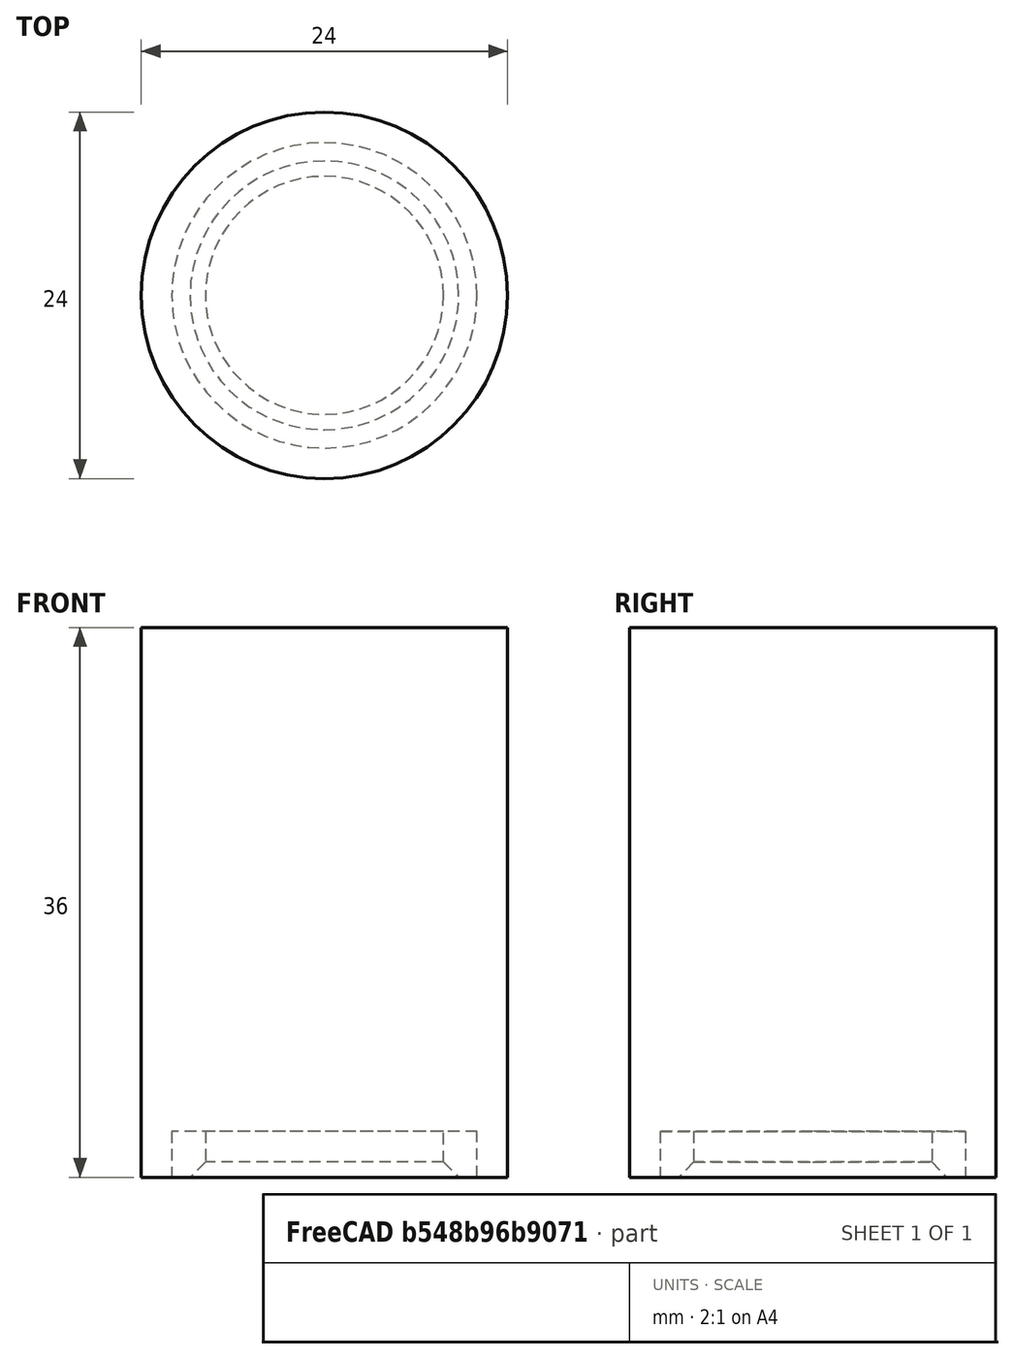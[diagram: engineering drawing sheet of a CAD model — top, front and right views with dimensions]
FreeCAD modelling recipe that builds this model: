
FCSTD DOCUMENT  (FreeCAD 0.20R25645 (Git))
Label: Brake Liquid Tester lid
License: All rights reserved
LicenseURL: http://en.wikipedia.org/wiki/All_rights_reserved
objects: Part::Cylinder×4, Part::Cut×2, Part::Chamfer×2, Part::MultiFuse×1, Part::Box×1
note: 10 computed .brp shape members not serialized (recipe doc carries the construction recipe); baked Part::Feature solids carry a one-line shape summary decoded from their .brp

FEATURE [Part::Cylinder] Cylinder
  Angle = 360
  AttacherType = Attacher::AttachEngine3D
  FirstAngle = 0
  Height = 28
  Radius = 10
  SecondAngle = 0
FEATURE [Part::Cylinder] Cylinder001
  Angle = 360
  AttacherType = Attacher::AttachEngine3D
  FirstAngle = 0
  Height = 12
  Radius = 7.8
  SecondAngle = 0
FEATURE [Part::Cylinder] Cylinder002
  Angle = 360
  AttacherType = Attacher::AttachEngine3D
  FirstAngle = 0
  Height = 12
  Placement = pos=(0,0,12) rot=(0,0,1;0rad)
  Radius = 5
  SecondAngle = 0
FEATURE [Part::Cylinder] Cylinder003
  Angle = 360
  AttacherType = Attacher::AttachEngine3D
  FirstAngle = 0
  Height = 36
  Radius = 12
  SecondAngle = 0
FEATURE [Part::MultiFuse] Fusion
  Shapes = -> [Cylinder001,Cylinder002]
FEATURE [Part::Cut] Cut
  Base = -> Cylinder
  Tool = -> Fusion
FEATURE [Part::Chamfer] Chamfer
  Base = -> Cut
  Edges = 1 edges r=2.7: [Edge7]
FEATURE [Part::Chamfer] Chamfer001
  Base = -> Chamfer
  Edges = 1 edges r=1: [Edge6]
FEATURE [Part::Box] Box  label="Cube"
  AttacherType = Attacher::AttachEngine3D
  Height = 36
  Length = 25
  Placement = pos=(-11,-13,3) rot=(0,0,1;0rad)
  Width = 25
FEATURE [Part::Cut] Cut001
  Base = -> Chamfer001
  Tool = -> Box
